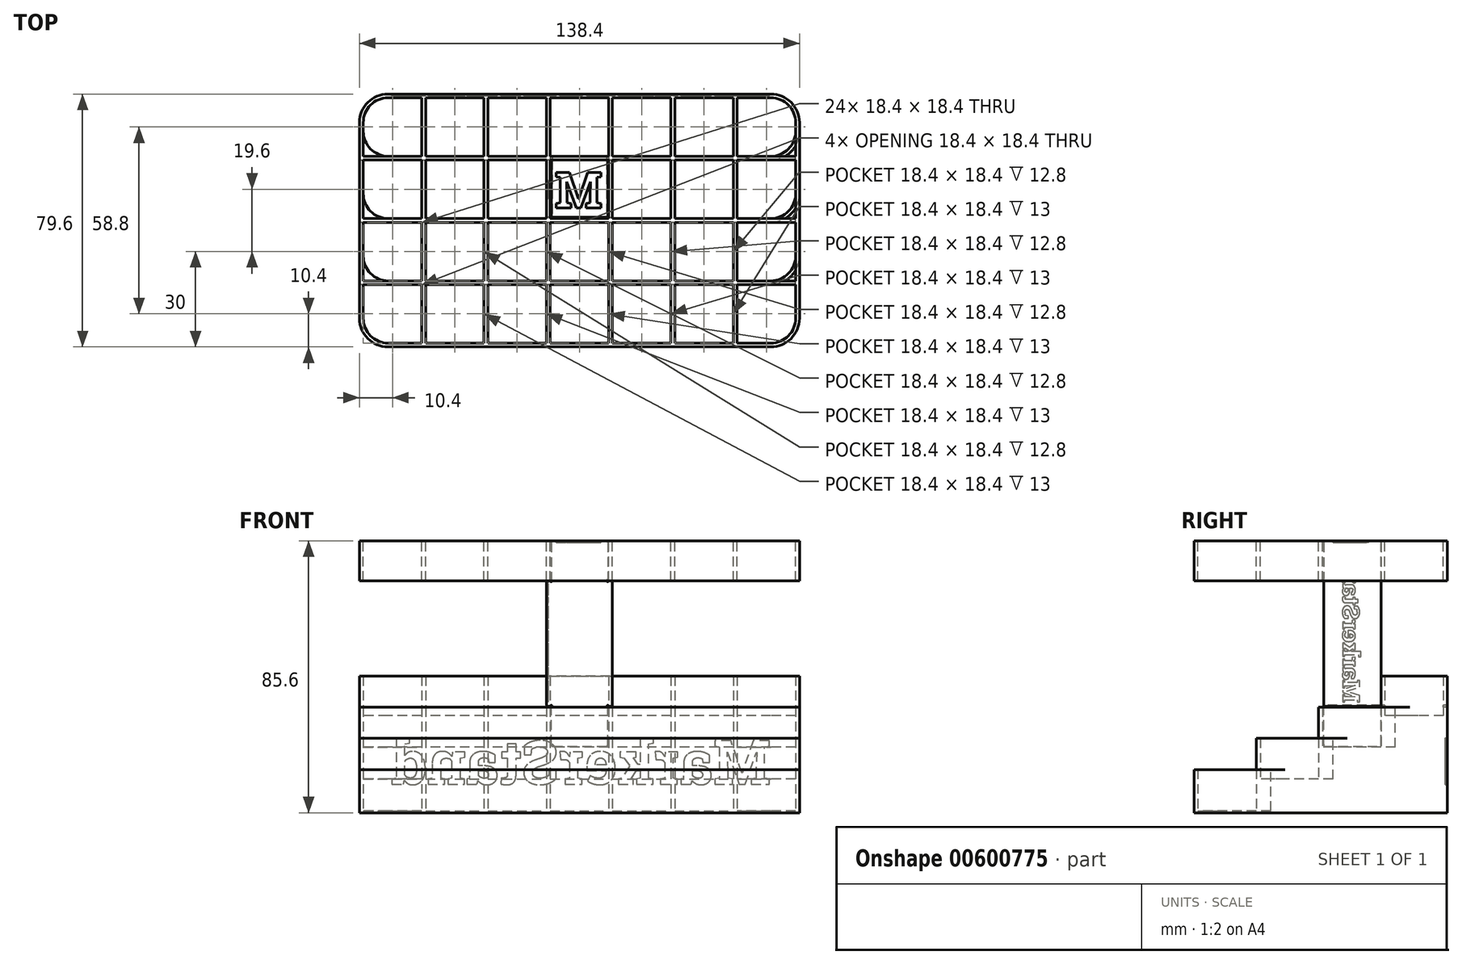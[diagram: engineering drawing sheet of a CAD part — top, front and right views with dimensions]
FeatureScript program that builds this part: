
annotation { "Feature Type Name" : "Feature", "Feature Type Description" : "" }
export const myFeature = defineFeature(function(context is Context, id is Id, definition is map)
    precondition{}
    {
        {
            var Q0;
            Q0=qCreatedBy(makeId("Top.planeOp"),FACE);
            var sketch = newSketch(context, id + "F0", { "sketchPlane" : qUnion([Q0])});
            skLineSegment(sketch, "E0.bottom", {"start": v(69.2, 39.8) * mm, "end": v(-69.2, 39.8) * mm});
            skLineSegment(sketch, "E0.top", {"start": v(69.2, -39.8) * mm, "end": v(-69.2, -39.8) * mm});
            skLineSegment(sketch, "E0.left", {"start": v(69.2, 39.8) * mm, "end": v(69.2, -39.8) * mm});
            skLineSegment(sketch, "E0.right", {"start": v(-69.2, 39.8) * mm, "end": v(-69.2, -39.8) * mm});
            skPoint(sketch, "E0.middle", {"position": v(0, 0) * mm});
            skLineSegment(sketch, "E1.bottom", {"start": v(-68, -38.6) * mm, "end": v(-49.6, -38.6) * mm});
            skLineSegment(sketch, "E1.top", {"start": v(-68, -20.2) * mm, "end": v(-49.6, -20.2) * mm});
            skLineSegment(sketch, "E1.left", {"start": v(-68, -38.6) * mm, "end": v(-68, -20.2) * mm});
            skLineSegment(sketch, "E1.right", {"start": v(-49.6, -38.6) * mm, "end": v(-49.6, -20.2) * mm});
            skLineSegment(sketch, "E2.0.1.0", {"start": v(-68, -19) * mm, "end": v(-68, -0.6) * mm});
            skLineSegment(sketch, "E2.0.1.1", {"start": v(-68, -19) * mm, "end": v(-49.6, -19) * mm});
            skLineSegment(sketch, "E2.0.1.2", {"start": v(-49.6, -19) * mm, "end": v(-49.6, -0.6) * mm});
            skLineSegment(sketch, "E2.0.1.3", {"start": v(-68, -0.6) * mm, "end": v(-49.6, -0.6) * mm});
            skLineSegment(sketch, "E2.0.2.0", {"start": v(-68, 0.6) * mm, "end": v(-68, 19) * mm});
            skLineSegment(sketch, "E2.0.2.1", {"start": v(-68, 0.6) * mm, "end": v(-49.6, 0.6) * mm});
            skLineSegment(sketch, "E2.0.2.2", {"start": v(-49.6, 0.6) * mm, "end": v(-49.6, 19) * mm});
            skLineSegment(sketch, "E2.0.2.3", {"start": v(-68, 19) * mm, "end": v(-49.6, 19) * mm});
            skLineSegment(sketch, "E2.0.3.0", {"start": v(-68, 20.2) * mm, "end": v(-68, 38.6) * mm});
            skLineSegment(sketch, "E2.0.3.1", {"start": v(-68, 20.2) * mm, "end": v(-49.6, 20.2) * mm});
            skLineSegment(sketch, "E2.0.3.2", {"start": v(-49.6, 20.2) * mm, "end": v(-49.6, 38.6) * mm});
            skLineSegment(sketch, "E2.0.3.3", {"start": v(-68, 38.6) * mm, "end": v(-49.6, 38.6) * mm});
            skLineSegment(sketch, "E2.1.0.0", {"start": v(-48.4, -38.6) * mm, "end": v(-48.4, -20.2) * mm});
            skLineSegment(sketch, "E2.1.0.1", {"start": v(-48.4, -38.6) * mm, "end": v(-30, -38.6) * mm});
            skLineSegment(sketch, "E2.1.0.2", {"start": v(-30, -38.6) * mm, "end": v(-30, -20.2) * mm});
            skLineSegment(sketch, "E2.1.0.3", {"start": v(-48.4, -20.2) * mm, "end": v(-30, -20.2) * mm});
            skLineSegment(sketch, "E2.1.1.0", {"start": v(-48.4, -19) * mm, "end": v(-48.4, -0.6) * mm});
            skLineSegment(sketch, "E2.1.1.1", {"start": v(-48.4, -19) * mm, "end": v(-30, -19) * mm});
            skLineSegment(sketch, "E2.1.1.2", {"start": v(-30, -19) * mm, "end": v(-30, -0.6) * mm});
            skLineSegment(sketch, "E2.1.1.3", {"start": v(-48.4, -0.6) * mm, "end": v(-30, -0.6) * mm});
            skLineSegment(sketch, "E2.1.2.0", {"start": v(-48.4, 0.6) * mm, "end": v(-48.4, 19) * mm});
            skLineSegment(sketch, "E2.1.2.1", {"start": v(-48.4, 0.6) * mm, "end": v(-30, 0.6) * mm});
            skLineSegment(sketch, "E2.1.2.2", {"start": v(-30, 0.6) * mm, "end": v(-30, 19) * mm});
            skLineSegment(sketch, "E2.1.2.3", {"start": v(-48.4, 19) * mm, "end": v(-30, 19) * mm});
            skLineSegment(sketch, "E2.1.3.0", {"start": v(-48.4, 20.2) * mm, "end": v(-48.4, 38.6) * mm});
            skLineSegment(sketch, "E2.1.3.1", {"start": v(-48.4, 20.2) * mm, "end": v(-30, 20.2) * mm});
            skLineSegment(sketch, "E2.1.3.2", {"start": v(-30, 20.2) * mm, "end": v(-30, 38.6) * mm});
            skLineSegment(sketch, "E2.1.3.3", {"start": v(-48.4, 38.6) * mm, "end": v(-30, 38.6) * mm});
            skLineSegment(sketch, "E2.2.0.0", {"start": v(-28.8, -38.6) * mm, "end": v(-28.8, -20.2) * mm});
            skLineSegment(sketch, "E2.2.0.1", {"start": v(-28.8, -38.6) * mm, "end": v(-10.4, -38.6) * mm});
            skLineSegment(sketch, "E2.2.0.2", {"start": v(-10.4, -38.6) * mm, "end": v(-10.4, -20.2) * mm});
            skLineSegment(sketch, "E2.2.0.3", {"start": v(-28.8, -20.2) * mm, "end": v(-10.4, -20.2) * mm});
            skLineSegment(sketch, "E2.2.1.0", {"start": v(-28.8, -19) * mm, "end": v(-28.8, -0.6) * mm});
            skLineSegment(sketch, "E2.2.1.1", {"start": v(-28.8, -19) * mm, "end": v(-10.4, -19) * mm});
            skLineSegment(sketch, "E2.2.1.2", {"start": v(-10.4, -19) * mm, "end": v(-10.4, -0.6) * mm});
            skLineSegment(sketch, "E2.2.1.3", {"start": v(-28.8, -0.6) * mm, "end": v(-10.4, -0.6) * mm});
            skLineSegment(sketch, "E2.2.2.0", {"start": v(-28.8, 0.6) * mm, "end": v(-28.8, 19) * mm});
            skLineSegment(sketch, "E2.2.2.1", {"start": v(-28.8, 0.6) * mm, "end": v(-10.4, 0.6) * mm});
            skLineSegment(sketch, "E2.2.2.2", {"start": v(-10.4, 0.6) * mm, "end": v(-10.4, 19) * mm});
            skLineSegment(sketch, "E2.2.2.3", {"start": v(-28.8, 19) * mm, "end": v(-10.4, 19) * mm});
            skLineSegment(sketch, "E2.2.3.0", {"start": v(-28.8, 20.2) * mm, "end": v(-28.8, 38.6) * mm});
            skLineSegment(sketch, "E2.2.3.1", {"start": v(-28.8, 20.2) * mm, "end": v(-10.4, 20.2) * mm});
            skLineSegment(sketch, "E2.2.3.2", {"start": v(-10.4, 20.2) * mm, "end": v(-10.4, 38.6) * mm});
            skLineSegment(sketch, "E2.2.3.3", {"start": v(-28.8, 38.6) * mm, "end": v(-10.4, 38.6) * mm});
            skLineSegment(sketch, "E2.3.0.0", {"start": v(-9.2, -38.6) * mm, "end": v(-9.2, -20.2) * mm});
            skLineSegment(sketch, "E2.3.0.1", {"start": v(-9.2, -38.6) * mm, "end": v(9.2, -38.6) * mm});
            skLineSegment(sketch, "E2.3.0.2", {"start": v(9.2, -38.6) * mm, "end": v(9.2, -20.2) * mm});
            skLineSegment(sketch, "E2.3.0.3", {"start": v(-9.2, -20.2) * mm, "end": v(9.2, -20.2) * mm});
            skLineSegment(sketch, "E2.3.1.0", {"start": v(-9.2, -19) * mm, "end": v(-9.2, -0.6) * mm});
            skLineSegment(sketch, "E2.3.1.1", {"start": v(-9.2, -19) * mm, "end": v(9.2, -19) * mm});
            skLineSegment(sketch, "E2.3.1.2", {"start": v(9.2, -19) * mm, "end": v(9.2, -0.6) * mm});
            skLineSegment(sketch, "E2.3.1.3", {"start": v(-9.2, -0.6) * mm, "end": v(9.2, -0.6) * mm});
            skLineSegment(sketch, "E2.3.2.0", {"start": v(-9.2, 0.6) * mm, "end": v(-9.2, 19) * mm});
            skLineSegment(sketch, "E2.3.2.1", {"start": v(-9.2, 0.6) * mm, "end": v(9.2, 0.6) * mm});
            skLineSegment(sketch, "E2.3.2.2", {"start": v(9.2, 0.6) * mm, "end": v(9.2, 19) * mm});
            skLineSegment(sketch, "E2.3.2.3", {"start": v(-9.2, 19) * mm, "end": v(9.2, 19) * mm});
            skLineSegment(sketch, "E2.3.3.0", {"start": v(-9.2, 20.2) * mm, "end": v(-9.2, 38.6) * mm});
            skLineSegment(sketch, "E2.3.3.1", {"start": v(-9.2, 20.2) * mm, "end": v(9.2, 20.2) * mm});
            skLineSegment(sketch, "E2.3.3.2", {"start": v(9.2, 20.2) * mm, "end": v(9.2, 38.6) * mm});
            skLineSegment(sketch, "E2.3.3.3", {"start": v(-9.2, 38.6) * mm, "end": v(9.2, 38.6) * mm});
            skLineSegment(sketch, "E2.4.0.0", {"start": v(10.4, -38.6) * mm, "end": v(10.4, -20.2) * mm});
            skLineSegment(sketch, "E2.4.0.1", {"start": v(10.4, -38.6) * mm, "end": v(28.8, -38.6) * mm});
            skLineSegment(sketch, "E2.4.0.2", {"start": v(28.8, -38.6) * mm, "end": v(28.8, -20.2) * mm});
            skLineSegment(sketch, "E2.4.0.3", {"start": v(10.4, -20.2) * mm, "end": v(28.8, -20.2) * mm});
            skLineSegment(sketch, "E2.4.1.0", {"start": v(10.4, -19) * mm, "end": v(10.4, -0.6) * mm});
            skLineSegment(sketch, "E2.4.1.1", {"start": v(10.4, -19) * mm, "end": v(28.8, -19) * mm});
            skLineSegment(sketch, "E2.4.1.2", {"start": v(28.8, -19) * mm, "end": v(28.8, -0.6) * mm});
            skLineSegment(sketch, "E2.4.1.3", {"start": v(10.4, -0.6) * mm, "end": v(28.8, -0.6) * mm});
            skLineSegment(sketch, "E2.4.2.0", {"start": v(10.4, 0.6) * mm, "end": v(10.4, 19) * mm});
            skLineSegment(sketch, "E2.4.2.1", {"start": v(10.4, 0.6) * mm, "end": v(28.8, 0.6) * mm});
            skLineSegment(sketch, "E2.4.2.2", {"start": v(28.8, 0.6) * mm, "end": v(28.8, 19) * mm});
            skLineSegment(sketch, "E2.4.2.3", {"start": v(10.4, 19) * mm, "end": v(28.8, 19) * mm});
            skLineSegment(sketch, "E2.4.3.0", {"start": v(10.4, 20.2) * mm, "end": v(10.4, 38.6) * mm});
            skLineSegment(sketch, "E2.4.3.1", {"start": v(10.4, 20.2) * mm, "end": v(28.8, 20.2) * mm});
            skLineSegment(sketch, "E2.4.3.2", {"start": v(28.8, 20.2) * mm, "end": v(28.8, 38.6) * mm});
            skLineSegment(sketch, "E2.4.3.3", {"start": v(10.4, 38.6) * mm, "end": v(28.8, 38.6) * mm});
            skLineSegment(sketch, "E2.5.0.0", {"start": v(30, -38.6) * mm, "end": v(30, -20.2) * mm});
            skLineSegment(sketch, "E2.5.0.1", {"start": v(30, -38.6) * mm, "end": v(48.4, -38.6) * mm});
            skLineSegment(sketch, "E2.5.0.2", {"start": v(48.4, -38.6) * mm, "end": v(48.4, -20.2) * mm});
            skLineSegment(sketch, "E2.5.0.3", {"start": v(30, -20.2) * mm, "end": v(48.4, -20.2) * mm});
            skLineSegment(sketch, "E2.5.1.0", {"start": v(30, -19) * mm, "end": v(30, -0.6) * mm});
            skLineSegment(sketch, "E2.5.1.1", {"start": v(30, -19) * mm, "end": v(48.4, -19) * mm});
            skLineSegment(sketch, "E2.5.1.2", {"start": v(48.4, -19) * mm, "end": v(48.4, -0.6) * mm});
            skLineSegment(sketch, "E2.5.1.3", {"start": v(30, -0.6) * mm, "end": v(48.4, -0.6) * mm});
            skLineSegment(sketch, "E2.5.2.0", {"start": v(30, 0.6) * mm, "end": v(30, 19) * mm});
            skLineSegment(sketch, "E2.5.2.1", {"start": v(30, 0.6) * mm, "end": v(48.4, 0.6) * mm});
            skLineSegment(sketch, "E2.5.2.2", {"start": v(48.4, 0.6) * mm, "end": v(48.4, 19) * mm});
            skLineSegment(sketch, "E2.5.2.3", {"start": v(30, 19) * mm, "end": v(48.4, 19) * mm});
            skLineSegment(sketch, "E2.5.3.0", {"start": v(30, 20.2) * mm, "end": v(30, 38.6) * mm});
            skLineSegment(sketch, "E2.5.3.1", {"start": v(30, 20.2) * mm, "end": v(48.4, 20.2) * mm});
            skLineSegment(sketch, "E2.5.3.2", {"start": v(48.4, 20.2) * mm, "end": v(48.4, 38.6) * mm});
            skLineSegment(sketch, "E2.5.3.3", {"start": v(30, 38.6) * mm, "end": v(48.4, 38.6) * mm});
            skLineSegment(sketch, "E2.6.0.0", {"start": v(49.6, -38.6) * mm, "end": v(49.6, -20.2) * mm});
            skLineSegment(sketch, "E2.6.0.1", {"start": v(49.6, -38.6) * mm, "end": v(68, -38.6) * mm});
            skLineSegment(sketch, "E2.6.0.2", {"start": v(68, -38.6) * mm, "end": v(68, -20.2) * mm});
            skLineSegment(sketch, "E2.6.0.3", {"start": v(49.6, -20.2) * mm, "end": v(68, -20.2) * mm});
            skLineSegment(sketch, "E2.6.1.0", {"start": v(49.6, -19) * mm, "end": v(49.6, -0.6) * mm});
            skLineSegment(sketch, "E2.6.1.1", {"start": v(49.6, -19) * mm, "end": v(68, -19) * mm});
            skLineSegment(sketch, "E2.6.1.2", {"start": v(68, -19) * mm, "end": v(68, -0.6) * mm});
            skLineSegment(sketch, "E2.6.1.3", {"start": v(49.6, -0.6) * mm, "end": v(68, -0.6) * mm});
            skLineSegment(sketch, "E2.6.2.0", {"start": v(49.6, 0.6) * mm, "end": v(49.6, 19) * mm});
            skLineSegment(sketch, "E2.6.2.1", {"start": v(49.6, 0.6) * mm, "end": v(68, 0.6) * mm});
            skLineSegment(sketch, "E2.6.2.2", {"start": v(68, 0.6) * mm, "end": v(68, 19) * mm});
            skLineSegment(sketch, "E2.6.2.3", {"start": v(49.6, 19) * mm, "end": v(68, 19) * mm});
            skLineSegment(sketch, "E2.6.3.0", {"start": v(49.6, 20.2) * mm, "end": v(49.6, 38.6) * mm});
            skLineSegment(sketch, "E2.6.3.1", {"start": v(49.6, 20.2) * mm, "end": v(68, 20.2) * mm});
            skLineSegment(sketch, "E2.6.3.2", {"start": v(68, 20.2) * mm, "end": v(68, 38.6) * mm});
            skLineSegment(sketch, "E2.6.3.3", {"start": v(49.6, 38.6) * mm, "end": v(68, 38.6) * mm});
            skLineSegment(sketch, "E2.direction1", {"start": v(-68, -38.6) * mm, "end": v(-48.4, -38.6) * mm, "construction": true});
            skLineSegment(sketch, "E2.direction2", {"start": v(-68, -38.6) * mm, "end": v(-68, -19) * mm, "construction": true});
            skSolve(sketch);
        }
        {
            var Q0;
            Q0=qSketchRegion(id+"F0",true);
            extrude(context, id + "F1", {"entities" : qUnion([Q0]), "depth" : 43 * mm, "offsetDistance" : 25 * mm});
        }
        {
            var Q0;
            Q0=makeQuery(id+"F1.opExtrude","SWEPT_FACE",FACE,{"disambiguationData":[OSD([sQuery(id+"F0.wireOp",EDGE,"E0.left")])]});
            var sketch = newSketch(context, id + "F2", { "sketchPlane" : qUnion([Q0])});
            skLineSegment(sketch, "E3", {"start": v(39.8, 0) * mm, "end": v(-39.8, 0) * mm});
            skLineSegment(sketch, "E4", {"start": v(-39.8, 0) * mm, "end": v(-39.8, 0.6) * mm});
            skLineSegment(sketch, "E5", {"start": v(-39.8, 0.6) * mm, "end": v(-20.2, 0.6) * mm});
            skLineSegment(sketch, "E6", {"start": v(-20.2, 0.6) * mm, "end": v(-20.2, 10.6) * mm});
            skLineSegment(sketch, "E7", {"start": v(-20.2, 10.6) * mm, "end": v(-0.6, 10.6) * mm});
            skLineSegment(sketch, "E8", {"start": v(-0.6, 10.6) * mm, "end": v(-0.6, 20.6) * mm});
            skLineSegment(sketch, "E9", {"start": v(-0.6, 20.6) * mm, "end": v(19, 20.6) * mm});
            skLineSegment(sketch, "E10", {"start": v(19, 20.6) * mm, "end": v(19, 30.6) * mm});
            skLineSegment(sketch, "E11", {"start": v(19, 30.6) * mm, "end": v(39.8, 30.6) * mm});
            skLineSegment(sketch, "E12", {"start": v(39.8, 30.6) * mm, "end": v(39.8, 0) * mm});
            skSolve(sketch);
        }
        {
            var Q0;
            Q0=qSketchRegion(id+"F2",true);
            var Q1;
            Q1=makeQuery(id+"F1.opExtrude","SWEPT_FACE",FACE,{"disambiguationData":[OSD([sQuery(id+"F0.wireOp",EDGE,"E0.right")])]});
            extrude(context, id + "F3", {"entities" : qUnion([Q0]), "operationType" : NewBodyOperationType.ADD, "endBound" : BoundingType.UP_TO_SURFACE, "oppositeDirection" : true, "depth" : 25 * mm, "endBoundEntityFace" : qUnion([Q1]), "offsetDistance" : 25 * mm});
        }
        {
            var Q0;
            Q0=makeQuery(id+"F1.opExtrude","SWEPT_FACE",FACE,{"disambiguationData":[OSD([sQuery(id+"F0.wireOp",EDGE,"E0.right")])]});
            var sketch = newSketch(context, id + "F4", { "sketchPlane" : qUnion([Q0])});
            skLineSegment(sketch, "E13", {"start": v(39.8, 43) * mm, "end": v(39.8, 13.6) * mm});
            skLineSegment(sketch, "E14", {"start": v(39.8, 13.6) * mm, "end": v(20.2, 13.6) * mm});
            skLineSegment(sketch, "E15", {"start": v(20.2, 13.6) * mm, "end": v(20.2, 23.4) * mm});
            skLineSegment(sketch, "E16", {"start": v(20.2, 23.4) * mm, "end": v(0.6, 23.4) * mm});
            skLineSegment(sketch, "E17", {"start": v(0.6, 23.4) * mm, "end": v(0.6, 33.2) * mm});
            skLineSegment(sketch, "E18", {"start": v(0.6, 33.2) * mm, "end": v(-19, 33.2) * mm});
            skLineSegment(sketch, "E19", {"start": v(-19, 33.2) * mm, "end": v(-19, 43) * mm});
            skLineSegment(sketch, "E20", {"start": v(-19, 43) * mm, "end": v(39.8, 43) * mm});
            skSolve(sketch);
        }
        {
            var Q0;
            Q0=qSketchRegion(id+"F4",true);
            extrude(context, id + "F5", {"entities" : qUnion([Q0]), "operationType" : NewBodyOperationType.REMOVE, "endBound" : BoundingType.THROUGH_ALL, "oppositeDirection" : true, "depth" : 25 * mm, "offsetDistance" : 25 * mm});
        }
        {
            var Q0;
            Q0=makeQuery(id+"F1.opExtrude","SWEPT_EDGE",EDGE,{"disambiguationData":[OSD([sQuery(id+"F0.wireOp",EDGE,"E2.6.3.2"),sQuery(id+"F0.wireOp",EDGE,"E2.6.3.3")])]});
            var Q1;
            Q1=makeQuery(id+"F1.opExtrude","SWEPT_EDGE",EDGE,{"disambiguationData":[OSD([sQuery(id+"F0.wireOp",EDGE,"E2.0.3.0"),sQuery(id+"F0.wireOp",EDGE,"E2.0.3.3")])]});
            var Q2;
            Q2=makeQuery(id+"F1.opExtrude","SWEPT_EDGE",EDGE,{"disambiguationData":[OSD([sQuery(id+"F0.wireOp",EDGE,"E2.6.0.1"),sQuery(id+"F0.wireOp",EDGE,"E2.6.0.2")])]});
            var Q3;
            Q3=makeQuery(id+"F1.opExtrude","SWEPT_EDGE",EDGE,{"disambiguationData":[OSD([sQuery(id+"F0.wireOp",EDGE,"E1.bottom"),sQuery(id+"F0.wireOp",EDGE,"E1.left")])]});
            var Q4;
            Q4=makeQuery(id+"F1.opExtrude","SWEPT_EDGE",EDGE,{"disambiguationData":[OSD([sQuery(id+"F0.wireOp",EDGE,"E2.6.1.1"),sQuery(id+"F0.wireOp",EDGE,"E2.6.1.2")])]});
            var Q5;
            Q5=makeQuery(id+"F1.opExtrude","SWEPT_EDGE",EDGE,{"disambiguationData":[OSD([sQuery(id+"F0.wireOp",EDGE,"E2.6.2.1"),sQuery(id+"F0.wireOp",EDGE,"E2.6.2.2")])]});
            var Q6;
            Q6=makeQuery(id+"F1.opExtrude","SWEPT_EDGE",EDGE,{"disambiguationData":[OSD([sQuery(id+"F0.wireOp",EDGE,"E2.0.2.0"),sQuery(id+"F0.wireOp",EDGE,"E2.0.2.1")])]});
            var Q7;
            Q7=makeQuery(id+"F1.opExtrude","SWEPT_EDGE",EDGE,{"disambiguationData":[OSD([sQuery(id+"F0.wireOp",EDGE,"E2.0.1.0"),sQuery(id+"F0.wireOp",EDGE,"E2.0.1.1")])]});
            var Q8;
            Q8=makeQuery(id+"F1.opExtrude","SWEPT_EDGE",EDGE,{"disambiguationData":[OSD([sQuery(id+"F0.wireOp",EDGE,"E2.6.3.1"),sQuery(id+"F0.wireOp",EDGE,"E2.6.3.2")])]});
            var Q9;
            Q9=makeQuery(id+"F1.opExtrude","SWEPT_EDGE",EDGE,{"disambiguationData":[OSD([sQuery(id+"F0.wireOp",EDGE,"E2.0.3.0"),sQuery(id+"F0.wireOp",EDGE,"E2.0.3.1")])]});
            fillet(context, id + "F6", {"entities" : qUnion([Q0, Q1, Q2, Q3, Q4, Q5, Q6, Q7, Q8, Q9]), "radius" : 7.85 * mm, "tangentPropagation" : true, "allowEdgeOverflow" : false});
        }
        {
            var Q0;
            Q0=makeQuery(id+"F1.opExtrude","SWEPT_EDGE",EDGE,{"disambiguationData":[OSD([sQuery(id+"F0.wireOp",EDGE,"E0.top"),sQuery(id+"F0.wireOp",EDGE,"E0.right")])]});
            var Q1;
            Q1=makeQuery(id+"F5.boolean.opBoolean","COPY",EDGE,{"derivedFrom":makeQuery(id+"F5.opExtrude","CAP_EDGE",EDGE,{"disambiguationData":[OSD([sQuery(id+"F4.wireOp",EDGE,"E15")])],"isStart":true})});
            var Q2;
            Q2=makeQuery(id+"F5.boolean.opBoolean","COPY",EDGE,{"derivedFrom":makeQuery(id+"F5.opExtrude","CAP_EDGE",EDGE,{"disambiguationData":[OSD([sQuery(id+"F4.wireOp",EDGE,"E17")])],"isStart":true})});
            var Q3;
            Q3=makeQuery(id+"F1.opExtrude","SWEPT_EDGE",EDGE,{"disambiguationData":[OSD([sQuery(id+"F0.wireOp",EDGE,"E0.bottom"),sQuery(id+"F0.wireOp",EDGE,"E0.right")])]});
            var Q4;
            Q4=makeQuery(id+"F1.opExtrude","SWEPT_EDGE",EDGE,{"disambiguationData":[OSD([sQuery(id+"F0.wireOp",EDGE,"E0.bottom"),sQuery(id+"F0.wireOp",EDGE,"E0.left")])]});
            var Q5;
            Q5=makeQuery(id+"F5.boolean.opBoolean","INTERSECT",EDGE,{"derivedFrom":[makeQuery(id+"F1.opExtrude","SWEPT_FACE",FACE,{"disambiguationData":[OSD([sQuery(id+"F0.wireOp",EDGE,"E0.left")])]}),makeQuery(id+"F5.opExtrude","SWEPT_FACE",FACE,{"disambiguationData":[OSD([sQuery(id+"F4.wireOp",EDGE,"E17")])]})]});
            var Q6;
            Q6=makeQuery(id+"F5.boolean.opBoolean","INTERSECT",EDGE,{"derivedFrom":[makeQuery(id+"F1.opExtrude","SWEPT_FACE",FACE,{"disambiguationData":[OSD([sQuery(id+"F0.wireOp",EDGE,"E0.left")])]}),makeQuery(id+"F5.opExtrude","SWEPT_FACE",FACE,{"disambiguationData":[OSD([sQuery(id+"F4.wireOp",EDGE,"E15")])]})]});
            var Q7;
            Q7=makeQuery(id+"F1.opExtrude","SWEPT_EDGE",EDGE,{"disambiguationData":[OSD([sQuery(id+"F0.wireOp",EDGE,"E0.top"),sQuery(id+"F0.wireOp",EDGE,"E0.left")])]});
            var Q8;
            Q8=makeQuery(id+"F5.boolean.opBoolean","INTERSECT",EDGE,{"derivedFrom":[makeQuery(id+"F1.opExtrude","SWEPT_FACE",FACE,{"disambiguationData":[OSD([sQuery(id+"F0.wireOp",EDGE,"E0.left")])]}),makeQuery(id+"F5.opExtrude","SWEPT_FACE",FACE,{"disambiguationData":[OSD([sQuery(id+"F4.wireOp",EDGE,"E19")])]})]});
            var Q9;
            Q9=makeQuery(id+"F5.boolean.opBoolean","COPY",EDGE,{"derivedFrom":makeQuery(id+"F5.opExtrude","CAP_EDGE",EDGE,{"disambiguationData":[OSD([sQuery(id+"F4.wireOp",EDGE,"E19")])],"isStart":true})});
            fillet(context, id + "F7", {"entities" : qUnion([Q0, Q1, Q2, Q3, Q4, Q5, Q6, Q7, Q8, Q9]), "radius" : 9 * mm, "tangentPropagation" : true, "allowEdgeOverflow" : false});
        }
        {
            var Q0;
            Q0=makeQuery(id+"F1.opExtrude","SWEPT_FACE",FACE,{"disambiguationData":[OSD([sQuery(id+"F0.wireOp",EDGE,"E0.bottom")])]});
            var sketch = newSketch(context, id + "F8", { "sketchPlane" : qUnion([Q0])});
            skLineSegment(sketch, "E21", {"start": v(0, 0) * mm, "end": v(0, 43) * mm, "construction": true});
            skText(sketch, "E22", { "text": "MarkerStand", "fontName": "RobotoSlab-Bold.ttf"});
            const initialGuessF8  = {"E22": [-0.0602, 0.009, 1, 0, 0.0138]};
            skSetInitialGuess(sketch, initialGuessF8);
            skSolve(sketch);
        }
        {
            var Q0;
            Q0=qSketchRegion(id+"F8",true);
            extrude(context, id + "F9", {"entities" : qUnion([Q0]), "operationType" : NewBodyOperationType.REMOVE, "oppositeDirection" : true, "depth" : 0.6 * mm, "offsetDistance" : 25 * mm});
        }
        {
            var Q0;
            Q0=makeQuery(id+"F5.boolean.opBoolean","MERGE",FACE,{"derivedFrom":[makeQuery(id+"F1.opExtrude","SWEPT_FACE",FACE,{"disambiguationData":[OSD([sQuery(id+"F0.wireOp",EDGE,"E2.0.2.3")])]}),makeQuery(id+"F1.opExtrude","SWEPT_FACE",FACE,{"disambiguationData":[OSD([sQuery(id+"F0.wireOp",EDGE,"E2.1.2.3")])]}),makeQuery(id+"F1.opExtrude","SWEPT_FACE",FACE,{"disambiguationData":[OSD([sQuery(id+"F0.wireOp",EDGE,"E2.2.2.3")])]}),makeQuery(id+"F1.opExtrude","SWEPT_FACE",FACE,{"disambiguationData":[OSD([sQuery(id+"F0.wireOp",EDGE,"E2.3.2.3")])]}),makeQuery(id+"F1.opExtrude","SWEPT_FACE",FACE,{"disambiguationData":[OSD([sQuery(id+"F0.wireOp",EDGE,"E2.4.2.3")])]}),makeQuery(id+"F1.opExtrude","SWEPT_FACE",FACE,{"disambiguationData":[OSD([sQuery(id+"F0.wireOp",EDGE,"E2.5.2.3")])]}),makeQuery(id+"F1.opExtrude","SWEPT_FACE",FACE,{"disambiguationData":[OSD([sQuery(id+"F0.wireOp",EDGE,"E2.6.2.3")])]}),makeQuery(id+"F5.opExtrude","SWEPT_FACE",FACE,{"disambiguationData":[OSD([sQuery(id+"F4.wireOp",EDGE,"E19")])]})]});
            var sketch = newSketch(context, id + "F10", { "sketchPlane" : qUnion([Q0])});
            skLineSegment(sketch, "E23", {"start": v(-8.9, 20.9) * mm, "end": v(8.9, 20.9) * mm});
            skLineSegment(sketch, "E24", {"start": v(8.9, 20.9) * mm, "end": v(8.9, 33.5) * mm});
            skLineSegment(sketch, "E25", {"start": v(8.9, 33.5) * mm, "end": v(10.4, 33.5) * mm});
            skLineSegment(sketch, "E26", {"start": v(10.4, 33.5) * mm, "end": v(10.4, 73) * mm});
            skLineSegment(sketch, "E27", {"start": v(-8.9, 20.9) * mm, "end": v(-8.9, 33.5) * mm});
            skLineSegment(sketch, "E28", {"start": v(-8.9, 33.5) * mm, "end": v(-10.4, 33.5) * mm});
            skLineSegment(sketch, "E29", {"start": v(-10.4, 33.5) * mm, "end": v(-10.4, 73) * mm});
            skLineSegment(sketch, "E30", {"start": v(-10.4, 53.25) * mm, "end": v(10.4, 53.25) * mm, "construction": true});
            skLineSegment(sketch, "E31.MirrorCS", {"start": v(-8.9, 73) * mm, "end": v(-10.4, 73) * mm});
            skLineSegment(sketch, "E32.MirrorCS", {"start": v(-8.9, 85.6) * mm, "end": v(-8.9, 73) * mm});
            skLineSegment(sketch, "E33.MirrorCS", {"start": v(-8.9, 85.6) * mm, "end": v(8.9, 85.6) * mm});
            skLineSegment(sketch, "E34.MirrorCS", {"start": v(8.9, 85.6) * mm, "end": v(8.9, 73) * mm});
            skLineSegment(sketch, "E35.MirrorCS", {"start": v(8.9, 73) * mm, "end": v(10.4, 73) * mm});
            skSolve(sketch);
        }
        {
            var Q0;
            Q0=qSketchRegion(id+"F10",true);
            extrude(context, id + "F11", {"entities" : qUnion([Q0]), "depth" : 18 * mm, "offsetDistance" : 25 * mm});
        }
        {
            var Q0;
            Q0=makeQuery(id+"F11.opExtrude","CAP_FACE",FACE,{"disambiguationData":[OSD([sQuery(id+"F10.wireOp",EDGE,"E23"),sQuery(id+"F10.wireOp",EDGE,"E24"),sQuery(id+"F10.wireOp",EDGE,"E25"),sQuery(id+"F10.wireOp",EDGE,"E26"),sQuery(id+"F10.wireOp",EDGE,"E27"),sQuery(id+"F10.wireOp",EDGE,"E28"),sQuery(id+"F10.wireOp",EDGE,"E29"),sQuery(id+"F10.wireOp",EDGE,"E31.MirrorCS"),sQuery(id+"F10.wireOp",EDGE,"E32.MirrorCS"),sQuery(id+"F10.wireOp",EDGE,"E33.MirrorCS"),sQuery(id+"F10.wireOp",EDGE,"E34.MirrorCS"),sQuery(id+"F10.wireOp",EDGE,"E35.MirrorCS")])],"isStart":false});
            var sketch = newSketch(context, id + "F12", { "sketchPlane" : qUnion([Q0])});
            skCircle(sketch, "E36", {"center": v(-8.9, 73) * mm, "radius": 0.3 * mm});
            skCircle(sketch, "E37", {"center": v(8.9, 73) * mm, "radius": 0.3 * mm});
            skCircle(sketch, "E38", {"center": v(8.9, 33.5) * mm, "radius": 0.3 * mm});
            skCircle(sketch, "E39", {"center": v(-8.9, 33.5) * mm, "radius": 0.3 * mm});
            skSolve(sketch);
        }
        {
            var Q0;
            Q0=qSketchRegion(id+"F12",true);
            extrude(context, id + "F13", {"entities" : qUnion([Q0]), "operationType" : NewBodyOperationType.REMOVE, "endBound" : BoundingType.THROUGH_ALL, "oppositeDirection" : true, "depth" : 25 * mm, "offsetDistance" : 25 * mm});
        }
        {
            var Q0;
            Q0=makeQuery(id+"F11.opExtrude","SWEPT_EDGE",EDGE,{"disambiguationData":[OSD([sQuery(id+"F10.wireOp",EDGE,"E32.MirrorCS"),sQuery(id+"F10.wireOp",EDGE,"E33.MirrorCS")])]});
            var Q1;
            Q1=makeQuery(id+"F11.opExtrude","SWEPT_EDGE",EDGE,{"disambiguationData":[OSD([sQuery(id+"F10.wireOp",EDGE,"E33.MirrorCS"),sQuery(id+"F10.wireOp",EDGE,"E34.MirrorCS")])]});
            var Q2;
            Q2=makeQuery(id+"F13.boolean.opBoolean","INTERSECT",EDGE,{"derivedFrom":[makeQuery(id+"F11.opExtrude","SWEPT_FACE",FACE,{"disambiguationData":[OSD([sQuery(id+"F10.wireOp",EDGE,"E31.MirrorCS")])]}),makeQuery(id+"F13.opExtrude","SWEPT_FACE",FACE,{"disambiguationData":[OSD([sQuery(id+"F12.wireOp",EDGE,"E36")])]})]});
            var Q3;
            Q3=makeQuery(id+"F13.boolean.opBoolean","INTERSECT",EDGE,{"derivedFrom":[makeQuery(id+"F11.opExtrude","SWEPT_FACE",FACE,{"disambiguationData":[OSD([sQuery(id+"F10.wireOp",EDGE,"E32.MirrorCS")])]}),makeQuery(id+"F13.opExtrude","SWEPT_FACE",FACE,{"disambiguationData":[OSD([sQuery(id+"F12.wireOp",EDGE,"E36")])]})]});
            var Q4;
            Q4=makeQuery(id+"F11.opExtrude","SWEPT_EDGE",EDGE,{"disambiguationData":[OSD([sQuery(id+"F10.wireOp",EDGE,"E29"),sQuery(id+"F10.wireOp",EDGE,"E31.MirrorCS")])]});
            var Q5;
            Q5=makeQuery(id+"F11.opExtrude","SWEPT_EDGE",EDGE,{"disambiguationData":[OSD([sQuery(id+"F10.wireOp",EDGE,"E26"),sQuery(id+"F10.wireOp",EDGE,"E35.MirrorCS")])]});
            var Q6;
            Q6=makeQuery(id+"F13.boolean.opBoolean","INTERSECT",EDGE,{"derivedFrom":[makeQuery(id+"F11.opExtrude","SWEPT_FACE",FACE,{"disambiguationData":[OSD([sQuery(id+"F10.wireOp",EDGE,"E35.MirrorCS")])]}),makeQuery(id+"F13.opExtrude","SWEPT_FACE",FACE,{"disambiguationData":[OSD([sQuery(id+"F12.wireOp",EDGE,"E37")])]})]});
            var Q7;
            Q7=makeQuery(id+"F13.boolean.opBoolean","INTERSECT",EDGE,{"derivedFrom":[makeQuery(id+"F11.opExtrude","SWEPT_FACE",FACE,{"disambiguationData":[OSD([sQuery(id+"F10.wireOp",EDGE,"E34.MirrorCS")])]}),makeQuery(id+"F13.opExtrude","SWEPT_FACE",FACE,{"disambiguationData":[OSD([sQuery(id+"F12.wireOp",EDGE,"E37")])]})]});
            var Q8;
            Q8=makeQuery(id+"F11.opExtrude","SWEPT_EDGE",EDGE,{"disambiguationData":[OSD([sQuery(id+"F10.wireOp",EDGE,"E23"),sQuery(id+"F10.wireOp",EDGE,"E27")])]});
            var Q9;
            Q9=makeQuery(id+"F11.opExtrude","SWEPT_EDGE",EDGE,{"disambiguationData":[OSD([sQuery(id+"F10.wireOp",EDGE,"E23"),sQuery(id+"F10.wireOp",EDGE,"E24")])]});
            var Q10;
            Q10=makeQuery(id+"F13.boolean.opBoolean","INTERSECT",EDGE,{"derivedFrom":[makeQuery(id+"F11.opExtrude","SWEPT_FACE",FACE,{"disambiguationData":[OSD([sQuery(id+"F10.wireOp",EDGE,"E25")])]}),makeQuery(id+"F13.opExtrude","SWEPT_FACE",FACE,{"disambiguationData":[OSD([sQuery(id+"F12.wireOp",EDGE,"E38")])]})]});
            var Q11;
            Q11=makeQuery(id+"F13.boolean.opBoolean","INTERSECT",EDGE,{"derivedFrom":[makeQuery(id+"F11.opExtrude","SWEPT_FACE",FACE,{"disambiguationData":[OSD([sQuery(id+"F10.wireOp",EDGE,"E28")])]}),makeQuery(id+"F13.opExtrude","SWEPT_FACE",FACE,{"disambiguationData":[OSD([sQuery(id+"F12.wireOp",EDGE,"E39")])]})]});
            var Q12;
            Q12=makeQuery(id+"F13.boolean.opBoolean","INTERSECT",EDGE,{"derivedFrom":[makeQuery(id+"F11.opExtrude","SWEPT_FACE",FACE,{"disambiguationData":[OSD([sQuery(id+"F10.wireOp",EDGE,"E27")])]}),makeQuery(id+"F13.opExtrude","SWEPT_FACE",FACE,{"disambiguationData":[OSD([sQuery(id+"F12.wireOp",EDGE,"E39")])]})]});
            var Q13;
            Q13=makeQuery(id+"F11.opExtrude","SWEPT_EDGE",EDGE,{"disambiguationData":[OSD([sQuery(id+"F10.wireOp",EDGE,"E28"),sQuery(id+"F10.wireOp",EDGE,"E29")])]});
            var Q14;
            Q14=makeQuery(id+"F11.opExtrude","SWEPT_EDGE",EDGE,{"disambiguationData":[OSD([sQuery(id+"F10.wireOp",EDGE,"E25"),sQuery(id+"F10.wireOp",EDGE,"E26")])]});
            var Q15;
            Q15=makeQuery(id+"F13.boolean.opBoolean","INTERSECT",EDGE,{"derivedFrom":[makeQuery(id+"F11.opExtrude","SWEPT_FACE",FACE,{"disambiguationData":[OSD([sQuery(id+"F10.wireOp",EDGE,"E24")])]}),makeQuery(id+"F13.opExtrude","SWEPT_FACE",FACE,{"disambiguationData":[OSD([sQuery(id+"F12.wireOp",EDGE,"E38")])]})]});
            fillet(context, id + "F14", {"entities" : qUnion([Q0, Q1, Q2, Q3, Q4, Q5, Q6, Q7, Q8, Q9, Q10, Q11, Q12, Q13, Q14, Q15]), "radius" : 0.6 * mm, "tangentPropagation" : true, "allowEdgeOverflow" : false});
        }
        {
            var Q0;
            Q0=makeQuery(id+"F11.opExtrude","SWEPT_FACE",FACE,{"disambiguationData":[OSD([sQuery(id+"F10.wireOp",EDGE,"E29")])]});
            var sketch = newSketch(context, id + "F15", { "sketchPlane" : qUnion([Q0])});
            skText(sketch, "E40", { "text": "MarkerStand", "fontName": "RobotoSlab-Bold.ttf"});
            skLineSegment(sketch, "E41", {"start": v(-1, 53.25) * mm, "end": v(-19, 53.25) * mm, "construction": true});
            skLineSegment(sketch, "E42", {"start": v(-10, 72.4) * mm, "end": v(-10, 34.1) * mm, "construction": true});
            skLineSegment(sketch, "E43", {"start": v(-9.7, 53.25) * mm, "end": v(-9.7, 71.8) * mm, "construction": true});
            const initialGuessF15  = {"E40": [-0.0069, 0.0347, 0, 1, 0.0054]};
            skSetInitialGuess(sketch, initialGuessF15);
            skSolve(sketch);
        }
        {
            var Q0;
            Q0=qSketchRegion(id+"F15",true);
            extrude(context, id + "F16", {"entities" : qUnion([Q0]), "operationType" : NewBodyOperationType.REMOVE, "oppositeDirection" : true, "depth" : 0.6 * mm, "offsetDistance" : 25 * mm});
        }
        {
            var Q0;
            Q0=makeQuery(id+"F11.opExtrude","SWEPT_FACE",FACE,{"disambiguationData":[OSD([sQuery(id+"F10.wireOp",EDGE,"E33.MirrorCS")])]});
            var sketch = newSketch(context, id + "F17", { "sketchPlane" : qUnion([Q0])});
            skText(sketch, "E44", { "text": "M", "fontName": "RobotoSlab-Bold.ttf"});
            skLineSegment(sketch, "E45", {"start": v(8.3, 10) * mm, "end": v(-8.3, 10) * mm, "construction": true});
            skLineSegment(sketch, "E46", {"start": v(0, 9.7) * mm, "end": v(7.7, 9.7) * mm, "construction": true});
            const initialGuessF17  = {"E44": [-0.0077, 0.00394, 1, 0, 0.01132]};
            skSetInitialGuess(sketch, initialGuessF17);
            skSolve(sketch);
        }
        {
            var Q0;
            Q0=qSketchRegion(id+"F17",true);
            extrude(context, id + "F18", {"entities" : qUnion([Q0]), "operationType" : NewBodyOperationType.REMOVE, "oppositeDirection" : true, "depth" : 0.6 * mm, "offsetDistance" : 25 * mm});
        }
        {
            var Q0;
            Q0=makeQuery(id+"F11.opExtrude","SWEPT_FACE",FACE,{"disambiguationData":[OSD([sQuery(id+"F10.wireOp",EDGE,"E33.MirrorCS")])]});
            var sketch = newSketch(context, id + "F19", { "sketchPlane" : qUnion([Q0])});
            skLineSegment(sketch, "E47.bottom", {"start": v(-69.2, -39.8) * mm, "end": v(69.2, -39.8) * mm});
            skLineSegment(sketch, "E47.top", {"start": v(-69.2, 39.8) * mm, "end": v(69.2, 39.8) * mm});
            skLineSegment(sketch, "E47.left", {"start": v(-69.2, -39.8) * mm, "end": v(-69.2, 39.8) * mm});
            skLineSegment(sketch, "E47.right", {"start": v(69.2, -39.8) * mm, "end": v(69.2, 39.8) * mm});
            skPoint(sketch, "E47.middle", {"position": v(0, 0) * mm});
            skLineSegment(sketch, "E48.bottom", {"start": v(-49.6, -20.2) * mm, "end": v(-68, -20.2) * mm});
            skLineSegment(sketch, "E48.top", {"start": v(-49.6, -38.6) * mm, "end": v(-68, -38.6) * mm});
            skLineSegment(sketch, "E48.left", {"start": v(-49.6, -20.2) * mm, "end": v(-49.6, -38.6) * mm});
            skLineSegment(sketch, "E48.right", {"start": v(-68, -20.2) * mm, "end": v(-68, -38.6) * mm});
            skLineSegment(sketch, "E49.0.1.0", {"start": v(-49.6, -0.6) * mm, "end": v(-68, -0.6) * mm});
            skLineSegment(sketch, "E49.0.1.1", {"start": v(-68, -0.6) * mm, "end": v(-68, -19) * mm});
            skLineSegment(sketch, "E49.0.1.2", {"start": v(-49.6, -19) * mm, "end": v(-68, -19) * mm});
            skLineSegment(sketch, "E49.0.1.3", {"start": v(-49.6, -0.6) * mm, "end": v(-49.6, -19) * mm});
            skLineSegment(sketch, "E49.0.2.0", {"start": v(-49.6, 19) * mm, "end": v(-68, 19) * mm});
            skLineSegment(sketch, "E49.0.2.1", {"start": v(-68, 19) * mm, "end": v(-68, 0.6) * mm});
            skLineSegment(sketch, "E49.0.2.2", {"start": v(-49.6, 0.6) * mm, "end": v(-68, 0.6) * mm});
            skLineSegment(sketch, "E49.0.2.3", {"start": v(-49.6, 19) * mm, "end": v(-49.6, 0.6) * mm});
            skLineSegment(sketch, "E49.0.3.0", {"start": v(-49.6, 38.6) * mm, "end": v(-68, 38.6) * mm});
            skLineSegment(sketch, "E49.0.3.1", {"start": v(-68, 38.6) * mm, "end": v(-68, 20.2) * mm});
            skLineSegment(sketch, "E49.0.3.2", {"start": v(-49.6, 20.2) * mm, "end": v(-68, 20.2) * mm});
            skLineSegment(sketch, "E49.0.3.3", {"start": v(-49.6, 38.6) * mm, "end": v(-49.6, 20.2) * mm});
            skLineSegment(sketch, "E49.1.0.0", {"start": v(-30, -20.2) * mm, "end": v(-48.4, -20.2) * mm});
            skLineSegment(sketch, "E49.1.0.1", {"start": v(-48.4, -20.2) * mm, "end": v(-48.4, -38.6) * mm});
            skLineSegment(sketch, "E49.1.0.2", {"start": v(-30, -38.6) * mm, "end": v(-48.4, -38.6) * mm});
            skLineSegment(sketch, "E49.1.0.3", {"start": v(-30, -20.2) * mm, "end": v(-30, -38.6) * mm});
            skLineSegment(sketch, "E49.1.1.0", {"start": v(-30, -0.6) * mm, "end": v(-48.4, -0.6) * mm});
            skLineSegment(sketch, "E49.1.1.1", {"start": v(-48.4, -0.6) * mm, "end": v(-48.4, -19) * mm});
            skLineSegment(sketch, "E49.1.1.2", {"start": v(-30, -19) * mm, "end": v(-48.4, -19) * mm});
            skLineSegment(sketch, "E49.1.1.3", {"start": v(-30, -0.6) * mm, "end": v(-30, -19) * mm});
            skLineSegment(sketch, "E49.1.2.0", {"start": v(-30, 19) * mm, "end": v(-48.4, 19) * mm});
            skLineSegment(sketch, "E49.1.2.1", {"start": v(-48.4, 19) * mm, "end": v(-48.4, 0.6) * mm});
            skLineSegment(sketch, "E49.1.2.2", {"start": v(-30, 0.6) * mm, "end": v(-48.4, 0.6) * mm});
            skLineSegment(sketch, "E49.1.2.3", {"start": v(-30, 19) * mm, "end": v(-30, 0.6) * mm});
            skLineSegment(sketch, "E49.1.3.0", {"start": v(-30, 38.6) * mm, "end": v(-48.4, 38.6) * mm});
            skLineSegment(sketch, "E49.1.3.1", {"start": v(-48.4, 38.6) * mm, "end": v(-48.4, 20.2) * mm});
            skLineSegment(sketch, "E49.1.3.2", {"start": v(-30, 20.2) * mm, "end": v(-48.4, 20.2) * mm});
            skLineSegment(sketch, "E49.1.3.3", {"start": v(-30, 38.6) * mm, "end": v(-30, 20.2) * mm});
            skLineSegment(sketch, "E49.2.0.0", {"start": v(-10.4, -20.2) * mm, "end": v(-28.8, -20.2) * mm});
            skLineSegment(sketch, "E49.2.0.1", {"start": v(-28.8, -20.2) * mm, "end": v(-28.8, -38.6) * mm});
            skLineSegment(sketch, "E49.2.0.2", {"start": v(-10.4, -38.6) * mm, "end": v(-28.8, -38.6) * mm});
            skLineSegment(sketch, "E49.2.0.3", {"start": v(-10.4, -20.2) * mm, "end": v(-10.4, -38.6) * mm});
            skLineSegment(sketch, "E49.2.1.0", {"start": v(-10.4, -0.6) * mm, "end": v(-28.8, -0.6) * mm});
            skLineSegment(sketch, "E49.2.1.1", {"start": v(-28.8, -0.6) * mm, "end": v(-28.8, -19) * mm});
            skLineSegment(sketch, "E49.2.1.2", {"start": v(-10.4, -19) * mm, "end": v(-28.8, -19) * mm});
            skLineSegment(sketch, "E49.2.1.3", {"start": v(-10.4, -0.6) * mm, "end": v(-10.4, -19) * mm});
            skLineSegment(sketch, "E49.2.2.0", {"start": v(-10.4, 19) * mm, "end": v(-28.8, 19) * mm});
            skLineSegment(sketch, "E49.2.2.1", {"start": v(-28.8, 19) * mm, "end": v(-28.8, 0.6) * mm});
            skLineSegment(sketch, "E49.2.2.2", {"start": v(-10.4, 0.6) * mm, "end": v(-28.8, 0.6) * mm});
            skLineSegment(sketch, "E49.2.2.3", {"start": v(-10.4, 19) * mm, "end": v(-10.4, 0.6) * mm});
            skLineSegment(sketch, "E49.2.3.0", {"start": v(-10.4, 38.6) * mm, "end": v(-28.8, 38.6) * mm});
            skLineSegment(sketch, "E49.2.3.1", {"start": v(-28.8, 38.6) * mm, "end": v(-28.8, 20.2) * mm});
            skLineSegment(sketch, "E49.2.3.2", {"start": v(-10.4, 20.2) * mm, "end": v(-28.8, 20.2) * mm});
            skLineSegment(sketch, "E49.2.3.3", {"start": v(-10.4, 38.6) * mm, "end": v(-10.4, 20.2) * mm});
            skLineSegment(sketch, "E49.3.0.0", {"start": v(9.2, -20.2) * mm, "end": v(-9.2, -20.2) * mm});
            skLineSegment(sketch, "E49.3.0.1", {"start": v(-9.2, -20.2) * mm, "end": v(-9.2, -38.6) * mm});
            skLineSegment(sketch, "E49.3.0.2", {"start": v(9.2, -38.6) * mm, "end": v(-9.2, -38.6) * mm});
            skLineSegment(sketch, "E49.3.0.3", {"start": v(9.2, -20.2) * mm, "end": v(9.2, -38.6) * mm});
            skLineSegment(sketch, "E49.3.1.0", {"start": v(9.2, -0.6) * mm, "end": v(-9.2, -0.6) * mm});
            skLineSegment(sketch, "E49.3.1.1", {"start": v(-9.2, -0.6) * mm, "end": v(-9.2, -19) * mm});
            skLineSegment(sketch, "E49.3.1.2", {"start": v(9.2, -19) * mm, "end": v(-9.2, -19) * mm});
            skLineSegment(sketch, "E49.3.1.3", {"start": v(9.2, -0.6) * mm, "end": v(9.2, -19) * mm});
            skLineSegment(sketch, "E49.3.2.0", {"start": v(9.2, 19) * mm, "end": v(-9.2, 19) * mm});
            skLineSegment(sketch, "E49.3.2.1", {"start": v(-9.2, 19) * mm, "end": v(-9.2, 0.6) * mm});
            skLineSegment(sketch, "E49.3.2.2", {"start": v(9.2, 0.6) * mm, "end": v(-9.2, 0.6) * mm});
            skLineSegment(sketch, "E49.3.2.3", {"start": v(9.2, 19) * mm, "end": v(9.2, 0.6) * mm});
            skLineSegment(sketch, "E49.3.3.0", {"start": v(9.2, 38.6) * mm, "end": v(-9.2, 38.6) * mm});
            skLineSegment(sketch, "E49.3.3.1", {"start": v(-9.2, 38.6) * mm, "end": v(-9.2, 20.2) * mm});
            skLineSegment(sketch, "E49.3.3.2", {"start": v(9.2, 20.2) * mm, "end": v(-9.2, 20.2) * mm});
            skLineSegment(sketch, "E49.3.3.3", {"start": v(9.2, 38.6) * mm, "end": v(9.2, 20.2) * mm});
            skLineSegment(sketch, "E49.4.0.0", {"start": v(28.8, -20.2) * mm, "end": v(10.4, -20.2) * mm});
            skLineSegment(sketch, "E49.4.0.1", {"start": v(10.4, -20.2) * mm, "end": v(10.4, -38.6) * mm});
            skLineSegment(sketch, "E49.4.0.2", {"start": v(28.8, -38.6) * mm, "end": v(10.4, -38.6) * mm});
            skLineSegment(sketch, "E49.4.0.3", {"start": v(28.8, -20.2) * mm, "end": v(28.8, -38.6) * mm});
            skLineSegment(sketch, "E49.4.1.0", {"start": v(28.8, -0.6) * mm, "end": v(10.4, -0.6) * mm});
            skLineSegment(sketch, "E49.4.1.1", {"start": v(10.4, -0.6) * mm, "end": v(10.4, -19) * mm});
            skLineSegment(sketch, "E49.4.1.2", {"start": v(28.8, -19) * mm, "end": v(10.4, -19) * mm});
            skLineSegment(sketch, "E49.4.1.3", {"start": v(28.8, -0.6) * mm, "end": v(28.8, -19) * mm});
            skLineSegment(sketch, "E49.4.2.0", {"start": v(28.8, 19) * mm, "end": v(10.4, 19) * mm});
            skLineSegment(sketch, "E49.4.2.1", {"start": v(10.4, 19) * mm, "end": v(10.4, 0.6) * mm});
            skLineSegment(sketch, "E49.4.2.2", {"start": v(28.8, 0.6) * mm, "end": v(10.4, 0.6) * mm});
            skLineSegment(sketch, "E49.4.2.3", {"start": v(28.8, 19) * mm, "end": v(28.8, 0.6) * mm});
            skLineSegment(sketch, "E49.4.3.0", {"start": v(28.8, 38.6) * mm, "end": v(10.4, 38.6) * mm});
            skLineSegment(sketch, "E49.4.3.1", {"start": v(10.4, 38.6) * mm, "end": v(10.4, 20.2) * mm});
            skLineSegment(sketch, "E49.4.3.2", {"start": v(28.8, 20.2) * mm, "end": v(10.4, 20.2) * mm});
            skLineSegment(sketch, "E49.4.3.3", {"start": v(28.8, 38.6) * mm, "end": v(28.8, 20.2) * mm});
            skLineSegment(sketch, "E49.5.0.0", {"start": v(48.4, -20.2) * mm, "end": v(30, -20.2) * mm});
            skLineSegment(sketch, "E49.5.0.1", {"start": v(30, -20.2) * mm, "end": v(30, -38.6) * mm});
            skLineSegment(sketch, "E49.5.0.2", {"start": v(48.4, -38.6) * mm, "end": v(30, -38.6) * mm});
            skLineSegment(sketch, "E49.5.0.3", {"start": v(48.4, -20.2) * mm, "end": v(48.4, -38.6) * mm});
            skLineSegment(sketch, "E49.5.1.0", {"start": v(48.4, -0.6) * mm, "end": v(30, -0.6) * mm});
            skLineSegment(sketch, "E49.5.1.1", {"start": v(30, -0.6) * mm, "end": v(30, -19) * mm});
            skLineSegment(sketch, "E49.5.1.2", {"start": v(48.4, -19) * mm, "end": v(30, -19) * mm});
            skLineSegment(sketch, "E49.5.1.3", {"start": v(48.4, -0.6) * mm, "end": v(48.4, -19) * mm});
            skLineSegment(sketch, "E49.5.2.0", {"start": v(48.4, 19) * mm, "end": v(30, 19) * mm});
            skLineSegment(sketch, "E49.5.2.1", {"start": v(30, 19) * mm, "end": v(30, 0.6) * mm});
            skLineSegment(sketch, "E49.5.2.2", {"start": v(48.4, 0.6) * mm, "end": v(30, 0.6) * mm});
            skLineSegment(sketch, "E49.5.2.3", {"start": v(48.4, 19) * mm, "end": v(48.4, 0.6) * mm});
            skLineSegment(sketch, "E49.5.3.0", {"start": v(48.4, 38.6) * mm, "end": v(30, 38.6) * mm});
            skLineSegment(sketch, "E49.5.3.1", {"start": v(30, 38.6) * mm, "end": v(30, 20.2) * mm});
            skLineSegment(sketch, "E49.5.3.2", {"start": v(48.4, 20.2) * mm, "end": v(30, 20.2) * mm});
            skLineSegment(sketch, "E49.5.3.3", {"start": v(48.4, 38.6) * mm, "end": v(48.4, 20.2) * mm});
            skLineSegment(sketch, "E49.6.0.0", {"start": v(68, -20.2) * mm, "end": v(49.6, -20.2) * mm});
            skLineSegment(sketch, "E49.6.0.1", {"start": v(49.6, -20.2) * mm, "end": v(49.6, -38.6) * mm});
            skLineSegment(sketch, "E49.6.0.2", {"start": v(68, -38.6) * mm, "end": v(49.6, -38.6) * mm});
            skLineSegment(sketch, "E49.6.0.3", {"start": v(68, -20.2) * mm, "end": v(68, -38.6) * mm});
            skLineSegment(sketch, "E49.6.1.0", {"start": v(68, -0.6) * mm, "end": v(49.6, -0.6) * mm});
            skLineSegment(sketch, "E49.6.1.1", {"start": v(49.6, -0.6) * mm, "end": v(49.6, -19) * mm});
            skLineSegment(sketch, "E49.6.1.2", {"start": v(68, -19) * mm, "end": v(49.6, -19) * mm});
            skLineSegment(sketch, "E49.6.1.3", {"start": v(68, -0.6) * mm, "end": v(68, -19) * mm});
            skLineSegment(sketch, "E49.6.2.0", {"start": v(68, 19) * mm, "end": v(49.6, 19) * mm});
            skLineSegment(sketch, "E49.6.2.1", {"start": v(49.6, 19) * mm, "end": v(49.6, 0.6) * mm});
            skLineSegment(sketch, "E49.6.2.2", {"start": v(68, 0.6) * mm, "end": v(49.6, 0.6) * mm});
            skLineSegment(sketch, "E49.6.2.3", {"start": v(68, 19) * mm, "end": v(68, 0.6) * mm});
            skLineSegment(sketch, "E49.6.3.0", {"start": v(68, 38.6) * mm, "end": v(49.6, 38.6) * mm});
            skLineSegment(sketch, "E49.6.3.1", {"start": v(49.6, 38.6) * mm, "end": v(49.6, 20.2) * mm});
            skLineSegment(sketch, "E49.6.3.2", {"start": v(68, 20.2) * mm, "end": v(49.6, 20.2) * mm});
            skLineSegment(sketch, "E49.6.3.3", {"start": v(68, 38.6) * mm, "end": v(68, 20.2) * mm});
            skLineSegment(sketch, "E49.direction1", {"start": v(-68, -38.6) * mm, "end": v(-48.4, -38.6) * mm, "construction": true});
            skLineSegment(sketch, "E49.direction2", {"start": v(-68, -38.6) * mm, "end": v(-68, -19) * mm, "construction": true});
            skSolve(sketch);
        }
        {
            var Q0;
            Q0=qSketchRegion(id+"F19",true);
            extrude(context, id + "F20", {"entities" : qUnion([Q0]), "oppositeDirection" : true, "depth" : 12.6 * mm, "offsetDistance" : 25 * mm});
        }
        {
            var Q0;
            Q0=makeQuery(id+"F20.opExtrude","SWEPT_EDGE",EDGE,{"disambiguationData":[OSD([sQuery(id+"F19.wireOp",EDGE,"E49.0.3.0"),sQuery(id+"F19.wireOp",EDGE,"E49.0.3.1")])]});
            var Q1;
            Q1=makeQuery(id+"F20.opExtrude","SWEPT_EDGE",EDGE,{"disambiguationData":[OSD([sQuery(id+"F19.wireOp",EDGE,"E49.6.3.0"),sQuery(id+"F19.wireOp",EDGE,"E49.6.3.3")])]});
            var Q2;
            Q2=makeQuery(id+"F20.opExtrude","SWEPT_EDGE",EDGE,{"disambiguationData":[OSD([sQuery(id+"F19.wireOp",EDGE,"E49.6.0.2"),sQuery(id+"F19.wireOp",EDGE,"E49.6.0.3")])]});
            var Q3;
            Q3=makeQuery(id+"F20.opExtrude","SWEPT_EDGE",EDGE,{"disambiguationData":[OSD([sQuery(id+"F19.wireOp",EDGE,"E48.top"),sQuery(id+"F19.wireOp",EDGE,"E48.right")])]});
            fillet(context, id + "F21", {"entities" : qUnion([Q0, Q1, Q2, Q3]), "radius" : 7.8 * mm, "tangentPropagation" : true, "allowEdgeOverflow" : false});
        }
        {
            var Q0;
            Q0=makeQuery(id+"F20.opExtrude","SWEPT_EDGE",EDGE,{"disambiguationData":[OSD([sQuery(id+"F19.wireOp",EDGE,"E47.bottom"),sQuery(id+"F19.wireOp",EDGE,"E47.right")])]});
            var Q1;
            Q1=makeQuery(id+"F20.opExtrude","SWEPT_EDGE",EDGE,{"disambiguationData":[OSD([sQuery(id+"F19.wireOp",EDGE,"E47.top"),sQuery(id+"F19.wireOp",EDGE,"E47.right")])]});
            var Q2;
            Q2=makeQuery(id+"F20.opExtrude","SWEPT_EDGE",EDGE,{"disambiguationData":[OSD([sQuery(id+"F19.wireOp",EDGE,"E47.top"),sQuery(id+"F19.wireOp",EDGE,"E47.left")])]});
            var Q3;
            Q3=makeQuery(id+"F20.opExtrude","SWEPT_EDGE",EDGE,{"disambiguationData":[OSD([sQuery(id+"F19.wireOp",EDGE,"E47.bottom"),sQuery(id+"F19.wireOp",EDGE,"E47.left")])]});
            fillet(context, id + "F22", {"entities" : qUnion([Q0, Q1, Q2, Q3]), "radius" : 9 * mm, "tangentPropagation" : true, "allowEdgeOverflow" : false});
        }
    });
